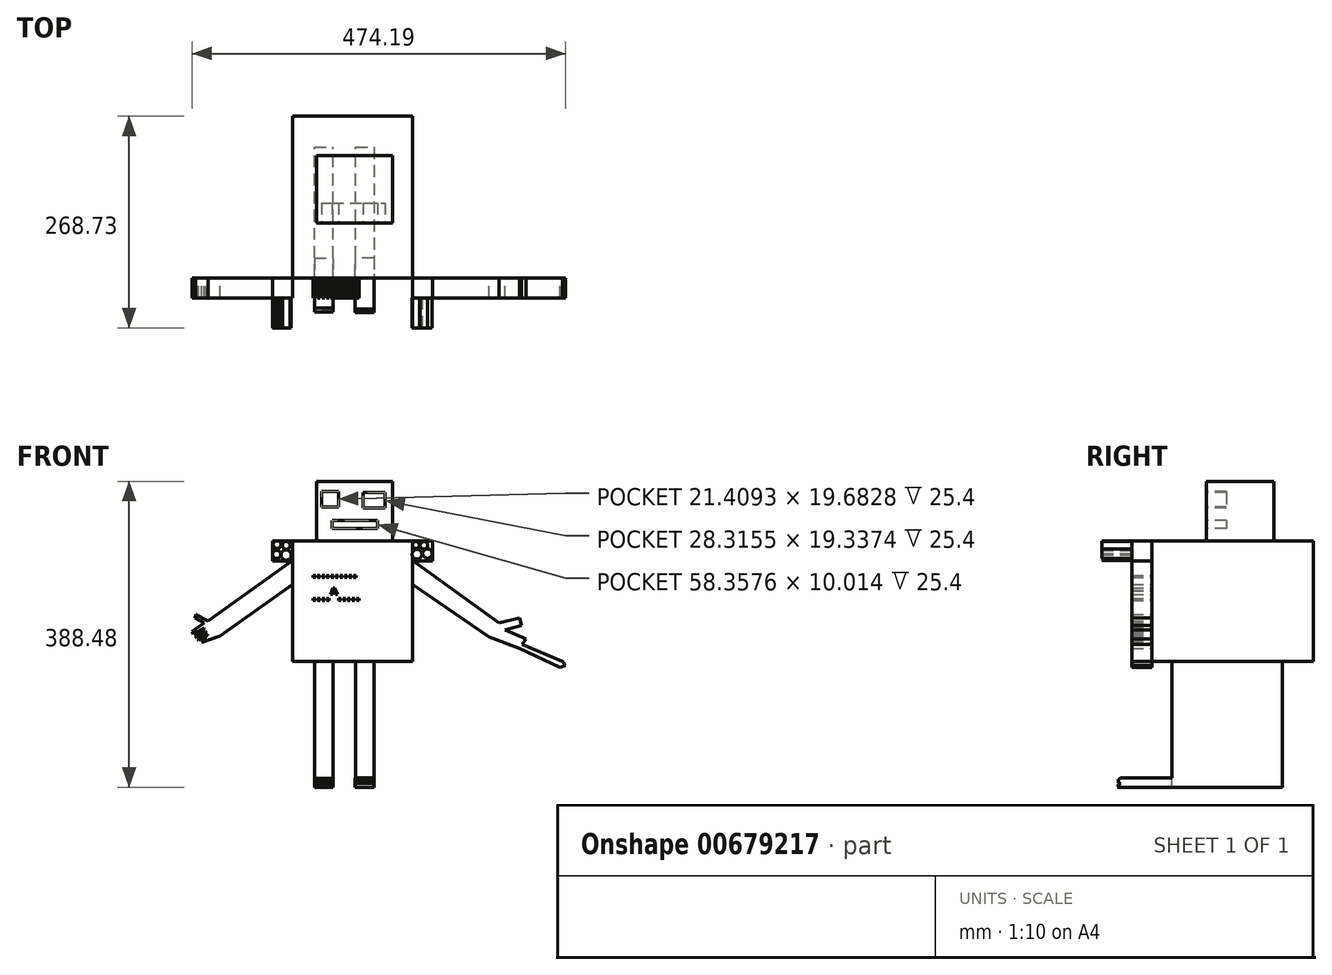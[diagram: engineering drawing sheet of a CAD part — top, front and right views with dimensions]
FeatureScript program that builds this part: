
annotation { "Feature Type Name" : "Feature", "Feature Type Description" : "" }
export const myFeature = defineFeature(function(context is Context, id is Id, definition is map)
    precondition{}
    {
        {
            var Q0;
            Q0=qCreatedBy(makeId("Front.planeOp"),FACE);
            var sketch = newSketch(context, id + "F0", { "sketchPlane" : qUnion([Q0])});
            skLineSegment(sketch, "E0.bottom", {"start": v(-75.78, 76.02) * mm, "end": v(76.26, 76.02) * mm});
            skLineSegment(sketch, "E0.top", {"start": v(-75.78, -76.75) * mm, "end": v(76.26, -76.75) * mm});
            skLineSegment(sketch, "E0.left", {"start": v(-75.78, 76.02) * mm, "end": v(-75.78, -76.75) * mm});
            skLineSegment(sketch, "E0.right", {"start": v(76.26, 76.02) * mm, "end": v(76.26, -76.75) * mm});
            skSolve(sketch);
        }
        {
            var Q0;
            Q0=makeQuery(id+"F0.imprint","IMPRINT",FACE,{"disambiguationData":[TD([[makeQuery(id+"F0.imprint","IMPRINT",EDGE,{"derivedFrom":sQuery(id+"F0.wireOp",EDGE,"E0.bottom")}),-1.0]])]});
            extrude(context, id + "F1", {"entities" : qUnion([Q0]), "depth" : 205.23 * mm, "offsetDistance" : 25.4 * mm});
        }
        {
            var Q0;
            Q0=makeQuery(id+"F1.opExtrude","CAP_FACE",FACE,{"disambiguationData":[OSD([sQuery(id+"F0.wireOp",EDGE,"E0.bottom"),sQuery(id+"F0.wireOp",EDGE,"E0.top"),sQuery(id+"F0.wireOp",EDGE,"E0.left"),sQuery(id+"F0.wireOp",EDGE,"E0.right")])],"isStart":false});
            var sketch = newSketch(context, id + "F2", { "sketchPlane" : qUnion([Q0])});
            skLineSegment(sketch, "E1", {"start": v(-75.78, 76.02) * mm, "end": v(-101.18, 76.02) * mm});
            skLineSegment(sketch, "E2", {"start": v(-101.18, 50.62) * mm, "end": v(-101.18, 76.02) * mm});
            skLineSegment(sketch, "E3", {"start": v(-101.18, 50.62) * mm, "end": v(-75.78, 50.62) * mm});
            skLineSegment(sketch, "E4", {"start": v(-75.78, 50.62) * mm, "end": v(-75.78, 50.62) * mm});
            skLineSegment(sketch, "E5", {"start": v(-75.78, 50.62) * mm, "end": v(-75.78, 76.02) * mm});
            skLineSegment(sketch, "E6", {"start": v(76.26, 76.02) * mm, "end": v(101.66, 76.02) * mm});
            skLineSegment(sketch, "E7", {"start": v(101.66, 76.02) * mm, "end": v(101.66, 50.62) * mm});
            skLineSegment(sketch, "E8", {"start": v(101.66, 50.62) * mm, "end": v(76.26, 50.62) * mm});
            skLineSegment(sketch, "E9", {"start": v(76.26, 50.62) * mm, "end": v(76.26, 76.02) * mm});
            skSolve(sketch);
        }
        {
            var Q0;
            Q0=makeQuery(id+"F2.imprint","IMPRINT",FACE,{"disambiguationData":[TD([[makeQuery(id+"F2.imprint","IMPRINT",EDGE,{"derivedFrom":sQuery(id+"F2.wireOp",EDGE,"E1")}),1.0]])]});
            var Q1;
            Q1=makeQuery(id+"F2.imprint","IMPRINT",FACE,{"disambiguationData":[TD([[makeQuery(id+"F2.imprint","IMPRINT",EDGE,{"derivedFrom":sQuery(id+"F2.wireOp",EDGE,"E6")}),-1.0]])]});
            extrude(context, id + "F3", {"entities" : qUnion([Q0, Q1]), "depth" : 25.4 * mm, "offsetDistance" : 25.4 * mm});
        }
        {
            var Q0;
            Q0=makeQuery(id+"F3.opExtrude","CAP_FACE",FACE,{"disambiguationData":[OSD([sQuery(id+"F2.wireOp",EDGE,"E1"),sQuery(id+"F2.wireOp",EDGE,"E2"),sQuery(id+"F2.wireOp",EDGE,"E3"),sQuery(id+"F2.wireOp",EDGE,"E5")])],"isStart":false});
            var sketch = newSketch(context, id + "F4", { "sketchPlane" : qUnion([Q0])});
            skCircle(sketch, "E10", {"center": v(-95.6, 71.34) * mm, "radius": 4.89 * mm});
            skCircle(sketch, "E11", {"center": v(-84.03, 70.36) * mm, "radius": 4.92 * mm});
            skCircle(sketch, "E12", {"center": v(-96.09, 59.03) * mm, "radius": 5.18 * mm});
            skCircle(sketch, "E13", {"center": v(-84.03, 58.05) * mm, "radius": 6.5 * mm});
            skCircle(sketch, "E14", {"center": v(80.67, 70.85) * mm, "radius": 4.44 * mm});
            skCircle(sketch, "E15", {"center": v(91.01, 70.36) * mm, "radius": 4.78 * mm});
            skCircle(sketch, "E16", {"center": v(82.15, 59.03) * mm, "radius": 6.12 * mm});
            skCircle(sketch, "E17", {"center": v(95.44, 60.02) * mm, "radius": 6 * mm});
            skSolve(sketch);
        }
        {
            var Q0;
            {var subQ0=sQuery(id+"F4.wireOp",EDGE,"E10");var subQ1=makeQuery(id+"F3.opExtrude","CAP_EDGE",EDGE,{"disambiguationData":[OSD([sQuery(id+"F2.wireOp",EDGE,"E1")])],"isStart":false});var subQ2=makeQuery(id+"F4.imprint","INTERSECT",VERTEX,{"disambiguationData":[OD(0.0)],"derivedFrom":[subQ1,subQ0]});Q0=makeQuery(id+"F4.imprint","IMPRINT",FACE,{"disambiguationData":[TD([[makeQuery(id+"F4.imprint","IMPRINT",EDGE,{"disambiguationData":[TD([[subQ2,1.0]])],"derivedFrom":subQ0}),1.0]])]});}
            var Q1;
            {var subQ0=sQuery(id+"F4.wireOp",EDGE,"E12");var subQ1=makeQuery(id+"F3.opExtrude","CAP_EDGE",EDGE,{"disambiguationData":[OSD([sQuery(id+"F2.wireOp",EDGE,"E2")])],"isStart":false});var subQ2=makeQuery(id+"F4.imprint","INTERSECT",VERTEX,{"disambiguationData":[OD(0.0)],"derivedFrom":[subQ1,subQ0]});Q1=makeQuery(id+"F4.imprint","IMPRINT",FACE,{"disambiguationData":[TD([[makeQuery(id+"F4.imprint","IMPRINT",EDGE,{"disambiguationData":[TD([[subQ2,1.0]])],"derivedFrom":subQ0}),1.0]])]});}
            var Q2;
            Q2=makeQuery(id+"F4.imprint","IMPRINT",FACE,{"disambiguationData":[TD([[makeQuery(id+"F4.imprint","IMPRINT",EDGE,{"derivedFrom":sQuery(id+"F4.wireOp",EDGE,"E13")}),1.0]])]});
            var Q3;
            Q3=makeQuery(id+"F4.imprint","IMPRINT",FACE,{"disambiguationData":[TD([[makeQuery(id+"F4.imprint","IMPRINT",EDGE,{"derivedFrom":sQuery(id+"F4.wireOp",EDGE,"E11")}),1.0]])]});
            var Q4;
            Q4=makeQuery(id+"F4.imprint","IMPRINT",FACE,{"disambiguationData":[TD([[makeQuery(id+"F4.imprint","IMPRINT",EDGE,{"derivedFrom":sQuery(id+"F4.wireOp",EDGE,"E14")}),1.0]])]});
            var Q5;
            Q5=makeQuery(id+"F4.imprint","IMPRINT",FACE,{"disambiguationData":[TD([[makeQuery(id+"F4.imprint","IMPRINT",EDGE,{"derivedFrom":sQuery(id+"F4.wireOp",EDGE,"E16")}),1.0]])]});
            var Q6;
            Q6=makeQuery(id+"F4.imprint","IMPRINT",FACE,{"disambiguationData":[TD([[makeQuery(id+"F4.imprint","IMPRINT",EDGE,{"derivedFrom":sQuery(id+"F4.wireOp",EDGE,"E15")}),1.0]])]});
            var Q7;
            Q7=makeQuery(id+"F4.imprint","IMPRINT",FACE,{"disambiguationData":[TD([[makeQuery(id+"F4.imprint","IMPRINT",EDGE,{"derivedFrom":sQuery(id+"F4.wireOp",EDGE,"E17")}),1.0]])]});
            extrude(context, id + "F5", {"entities" : qUnion([Q0, Q1, Q2, Q3, Q4, Q5, Q6, Q7]), "depth" : 38.1 * mm, "offsetDistance" : 25.4 * mm});
        }
        {
            var Q0;
            Q0=makeQuery(id+"F1.opExtrude","CAP_FACE",FACE,{"disambiguationData":[OSD([sQuery(id+"F0.wireOp",EDGE,"E0.bottom"),sQuery(id+"F0.wireOp",EDGE,"E0.top"),sQuery(id+"F0.wireOp",EDGE,"E0.left"),sQuery(id+"F0.wireOp",EDGE,"E0.right")])],"isStart":false});
            var sketch = newSketch(context, id + "F6", { "sketchPlane" : qUnion([Q0])});
            skText(sketch, "E18", { "text": "..........\n....^.....", "fontName": "RobotoSlab-Bold.ttf"});
            const initialGuessF6  = {"E18": [-0.051, 0.02956, 1, 0, 0.016]};
            skSetInitialGuess(sketch, initialGuessF6);
            skSolve(sketch);
        }
        {
            var Q0;
            Q0 = qSketchRegion(id + "F6", true);
            extrude(context, id + "F7", {"entities" : qUnion([Q0]), "operationType" : NewBodyOperationType.ADD, "depth" : 25.4 * mm, "offsetDistance" : 25.4 * mm});
        }
        {
            var Q0;
            Q0=makeQuery(id+"F1.opExtrude","SWEPT_FACE",FACE,{"disambiguationData":[OSD([sQuery(id+"F0.wireOp",EDGE,"E0.top")])]});
            var sketch = newSketch(context, id + "F8", { "sketchPlane" : qUnion([Q0])});
            skLineSegment(sketch, "E19", {"start": v(-48.14, 179.76) * mm, "end": v(-48.14, 135.43) * mm});
            skLineSegment(sketch, "E20", {"start": v(-48.14, 179.76) * mm, "end": v(-24.7, 179.76) * mm});
            skLineSegment(sketch, "E21", {"start": v(-24.7, 179.76) * mm, "end": v(-24.7, 39.1) * mm});
            skLineSegment(sketch, "E22", {"start": v(-48.14, 39.1) * mm, "end": v(-48.14, 135.43) * mm});
            skLineSegment(sketch, "E23", {"start": v(-48.14, 39.1) * mm, "end": v(-24.7, 39.1) * mm});
            skLineSegment(sketch, "E24", {"start": v(4.3, 179.76) * mm, "end": v(4.3, 39.1) * mm});
            skLineSegment(sketch, "E25", {"start": v(4.3, 39.1) * mm, "end": v(27.3, 39.1) * mm});
            skLineSegment(sketch, "E26", {"start": v(27.3, 39.1) * mm, "end": v(27.3, 179.76) * mm});
            skLineSegment(sketch, "E27", {"start": v(27.3, 179.76) * mm, "end": v(4.3, 179.76) * mm});
            skSolve(sketch);
        }
        {
            var Q0;
            Q0=makeQuery(id+"F8.imprint","IMPRINT",FACE,{"disambiguationData":[TD([[makeQuery(id+"F8.imprint","IMPRINT",EDGE,{"derivedFrom":sQuery(id+"F8.wireOp",EDGE,"E19")}),1.0]])]});
            var Q1;
            Q1=makeQuery(id+"F8.imprint","IMPRINT",FACE,{"disambiguationData":[TD([[makeQuery(id+"F8.imprint","IMPRINT",EDGE,{"derivedFrom":sQuery(id+"F8.wireOp",EDGE,"E24")}),1.0]])]});
            extrude(context, id + "F9", {"entities" : qUnion([Q0, Q1]), "operationType" : NewBodyOperationType.ADD, "depth" : 160.02 * mm, "offsetDistance" : 25.4 * mm});
        }
        {
            var Q0;
            Q0=makeQuery(id+"F9.opExtrude","SWEPT_FACE",FACE,{"disambiguationData":[OSD([sQuery(id+"F8.wireOp",EDGE,"E26")])]});
            var sketch = newSketch(context, id + "F10", { "sketchPlane" : qUnion([Q0])});
            skLineSegment(sketch, "E28", {"start": v(-176.13, -225.1) * mm, "end": v(-245.06, -225.1) * mm});
            skLineSegment(sketch, "E29", {"start": v(-245.06, -225.1) * mm, "end": v(-248.62, -229.17) * mm});
            skLineSegment(sketch, "E30", {"start": v(-248.62, -229.17) * mm, "end": v(-245.06, -232.28) * mm});
            skLineSegment(sketch, "E31", {"start": v(-245.06, -232.28) * mm, "end": v(-248.98, -236.77) * mm});
            skLineSegment(sketch, "E32", {"start": v(-248.98, -236.77) * mm, "end": v(-179.76, -236.77) * mm});
            skLineSegment(sketch, "E33", {"start": v(-179.76, -236.77) * mm, "end": v(-176.13, -225.1) * mm});
            skSolve(sketch);
        }
        {
            var Q0;
            {var subQ0=sQuery(id+"F10.wireOp",EDGE,"E29");Q0=makeQuery(id+"F10.imprint","IMPRINT",FACE,{"disambiguationData":[TD([[makeQuery(id+"F10.imprint","IMPRINT",EDGE,{"derivedFrom":subQ0}),1.0]])]});}
            extrude(context, id + "F11", {"entities" : qUnion([Q0]), "operationType" : NewBodyOperationType.ADD, "oppositeDirection" : true, "depth" : 24.13 * mm, "offsetDistance" : 25.4 * mm});
        }
        {
            var Q0;
            Q0=makeQuery(id+"F9.opExtrude","SWEPT_FACE",FACE,{"disambiguationData":[OSD([sQuery(id+"F8.wireOp",EDGE,"E19"),sQuery(id+"F8.wireOp",EDGE,"E22")])]});
            var sketch = newSketch(context, id + "F12", { "sketchPlane" : qUnion([Q0])});
            skLineSegment(sketch, "E34", {"start": v(177.82, -225.49) * mm, "end": v(243.67, -225.49) * mm});
            skLineSegment(sketch, "E35", {"start": v(243.67, -225.49) * mm, "end": v(248.67, -228.82) * mm});
            skLineSegment(sketch, "E36", {"start": v(248.67, -228.82) * mm, "end": v(245.72, -233.24) * mm});
            skLineSegment(sketch, "E37", {"start": v(245.72, -233.24) * mm, "end": v(248.67, -235.21) * mm});
            skLineSegment(sketch, "E38", {"start": v(248.67, -235.21) * mm, "end": v(179.76, -236.77) * mm});
            skLineSegment(sketch, "E39", {"start": v(179.76, -236.77) * mm, "end": v(177.82, -225.49) * mm});
            skSolve(sketch);
        }
        {
            var Q0;
            {var subQ0=sQuery(id+"F12.wireOp",EDGE,"E35");Q0=makeQuery(id+"F12.imprint","IMPRINT",FACE,{"disambiguationData":[TD([[makeQuery(id+"F12.imprint","IMPRINT",EDGE,{"derivedFrom":subQ0}),-1.0]])]});}
            extrude(context, id + "F13", {"entities" : qUnion([Q0]), "operationType" : NewBodyOperationType.ADD, "oppositeDirection" : true, "depth" : 23.88 * mm, "offsetDistance" : 25.4 * mm});
        }
        {
            var Q0;
            Q0=makeQuery(id+"F1.opExtrude","SWEPT_FACE",FACE,{"disambiguationData":[OSD([sQuery(id+"F0.wireOp",EDGE,"E0.bottom")])]});
            var sketch = newSketch(context, id + "F14", { "sketchPlane" : qUnion([Q0])});
            skLineSegment(sketch, "E40.bottom", {"start": v(-45.76, -49.95) * mm, "end": v(51.15, -49.95) * mm});
            skLineSegment(sketch, "E40.top", {"start": v(-45.76, -135.53) * mm, "end": v(51.15, -135.53) * mm});
            skLineSegment(sketch, "E40.left", {"start": v(-45.76, -49.95) * mm, "end": v(-45.76, -135.53) * mm});
            skLineSegment(sketch, "E40.right", {"start": v(51.15, -49.95) * mm, "end": v(51.15, -135.53) * mm});
            skSolve(sketch);
        }
        {
            var Q0;
            Q0=makeQuery(id+"F14.imprint","IMPRINT",FACE,{"disambiguationData":[TD([[makeQuery(id+"F14.imprint","IMPRINT",EDGE,{"derivedFrom":sQuery(id+"F14.wireOp",EDGE,"E40.bottom")}),-1.0]])]});
            extrude(context, id + "F15", {"entities" : qUnion([Q0]), "operationType" : NewBodyOperationType.ADD, "depth" : 75.7 * mm, "offsetDistance" : 25.4 * mm});
        }
        {
            var Q0;
            Q0=makeQuery(id+"F15.opExtrude","SWEPT_FACE",FACE,{"disambiguationData":[OSD([sQuery(id+"F14.wireOp",EDGE,"E40.top")])]});
            var sketch = newSketch(context, id + "F16", { "sketchPlane" : qUnion([Q0])});
            skLineSegment(sketch, "E41.bottom", {"start": v(-39.15, 139.13) * mm, "end": v(-17.74, 139.13) * mm});
            skLineSegment(sketch, "E41.top", {"start": v(-39.15, 119.44) * mm, "end": v(-17.74, 119.44) * mm});
            skLineSegment(sketch, "E41.left", {"start": v(-39.15, 139.13) * mm, "end": v(-39.15, 119.44) * mm});
            skLineSegment(sketch, "E41.right", {"start": v(-17.74, 139.13) * mm, "end": v(-17.74, 119.44) * mm});
            skLineSegment(sketch, "E42.bottom", {"start": v(13.34, 137.4) * mm, "end": v(41.66, 137.4) * mm});
            skLineSegment(sketch, "E42.top", {"start": v(13.34, 118.06) * mm, "end": v(41.66, 118.06) * mm});
            skLineSegment(sketch, "E42.left", {"start": v(13.34, 137.4) * mm, "end": v(13.34, 118.06) * mm});
            skLineSegment(sketch, "E42.right", {"start": v(41.66, 137.4) * mm, "end": v(41.66, 118.06) * mm});
            skLineSegment(sketch, "E43.bottom", {"start": v(-26.02, 102.18) * mm, "end": v(32.33, 102.18) * mm});
            skLineSegment(sketch, "E43.top", {"start": v(-26.02, 92.16) * mm, "end": v(32.33, 92.16) * mm});
            skLineSegment(sketch, "E43.left", {"start": v(-26.02, 102.18) * mm, "end": v(-26.02, 92.16) * mm});
            skLineSegment(sketch, "E43.right", {"start": v(32.33, 102.18) * mm, "end": v(32.33, 92.16) * mm});
            skSolve(sketch);
        }
        {
            var Q0;
            Q0=makeQuery(id+"F16.imprint","IMPRINT",FACE,{"disambiguationData":[TD([[makeQuery(id+"F16.imprint","IMPRINT",EDGE,{"derivedFrom":sQuery(id+"F16.wireOp",EDGE,"E41.bottom")}),-1.0]])]});
            var Q1;
            Q1=makeQuery(id+"F16.imprint","IMPRINT",FACE,{"disambiguationData":[TD([[makeQuery(id+"F16.imprint","IMPRINT",EDGE,{"derivedFrom":sQuery(id+"F16.wireOp",EDGE,"E42.bottom")}),-1.0]])]});
            var Q2;
            Q2=makeQuery(id+"F16.imprint","IMPRINT",FACE,{"disambiguationData":[TD([[makeQuery(id+"F16.imprint","IMPRINT",EDGE,{"derivedFrom":sQuery(id+"F16.wireOp",EDGE,"E43.bottom")}),-1.0]])]});
            extrude(context, id + "F17", {"entities" : qUnion([Q0, Q1, Q2]), "operationType" : NewBodyOperationType.REMOVE, "oppositeDirection" : true, "depth" : 25.4 * mm, "offsetDistance" : 25.4 * mm});
        }
        {
            var Q0;
            Q0=makeQuery(id+"F1.opExtrude","CAP_FACE",FACE,{"disambiguationData":[OSD([sQuery(id+"F0.wireOp",EDGE,"E0.bottom"),sQuery(id+"F0.wireOp",EDGE,"E0.top"),sQuery(id+"F0.wireOp",EDGE,"E0.left"),sQuery(id+"F0.wireOp",EDGE,"E0.right")])],"isStart":false});
            var sketch = newSketch(context, id + "F18", { "sketchPlane" : qUnion([Q0])});
            skLineSegment(sketch, "E44", {"start": v(-75.78, 51.25) * mm, "end": v(-183.4, -25.82) * mm});
            skLineSegment(sketch, "E45", {"start": v(-183.4, -25.82) * mm, "end": v(-169.02, -45.9) * mm});
            skLineSegment(sketch, "E46", {"start": v(-168.22, -44.79) * mm, "end": v(-75.78, 20.6) * mm});
            skLineSegment(sketch, "E47", {"start": v(-183.4, -25.82) * mm, "end": v(-198.82, -17.33) * mm});
            skLineSegment(sketch, "E48", {"start": v(-198.82, -17.33) * mm, "end": v(-199.93, -21.65) * mm});
            skLineSegment(sketch, "E49", {"start": v(-199.93, -21.65) * mm, "end": v(-188.52, -28.41) * mm});
            skLineSegment(sketch, "E50", {"start": v(-188.52, -28.41) * mm, "end": v(-203.49, -39.13) * mm});
            skLineSegment(sketch, "E51", {"start": v(-203.49, -39.13) * mm, "end": v(-201.42, -42.01) * mm});
            skLineSegment(sketch, "E52", {"start": v(-201.42, -42.01) * mm, "end": v(-188.52, -34.3) * mm});
            skLineSegment(sketch, "E53", {"start": v(-188.52, -34.3) * mm, "end": v(-187.41, -35.84) * mm});
            skLineSegment(sketch, "E54", {"start": v(-187.41, -35.84) * mm, "end": v(-199.9, -44.79) * mm});
            skLineSegment(sketch, "E55", {"start": v(-199.9, -44.79) * mm, "end": v(-198.1, -47.31) * mm});
            skLineSegment(sketch, "E56", {"start": v(-198.1, -47.31) * mm, "end": v(-186.67, -39.13) * mm});
            skLineSegment(sketch, "E57", {"start": v(-186.67, -39.13) * mm, "end": v(-185.47, -40.8) * mm});
            skLineSegment(sketch, "E58", {"start": v(-185.47, -40.8) * mm, "end": v(-196.5, -48.7) * mm});
            skLineSegment(sketch, "E59", {"start": v(-196.5, -48.7) * mm, "end": v(-195.15, -50.6) * mm});
            skLineSegment(sketch, "E60", {"start": v(-195.15, -50.6) * mm, "end": v(-183.4, -42.18) * mm});
            skLineSegment(sketch, "E61", {"start": v(-183.4, -42.18) * mm, "end": v(-191.24, -53.16) * mm});
            skLineSegment(sketch, "E62", {"start": v(-191.24, -53.16) * mm, "end": v(-168.22, -44.79) * mm});
            skLineSegment(sketch, "E63", {"start": v(76.26, 51.25) * mm, "end": v(186.2, -28.41) * mm});
            skLineSegment(sketch, "E64", {"start": v(186.2, -28.41) * mm, "end": v(173.53, -45.9) * mm});
            skLineSegment(sketch, "E65", {"start": v(173.53, -45.9) * mm, "end": v(76.26, 20.6) * mm});
            skLineSegment(sketch, "E66", {"start": v(76.26, 20.6) * mm, "end": v(76.26, 51.25) * mm});
            skLineSegment(sketch, "E67", {"start": v(186.2, -28.41) * mm, "end": v(212.58, -21.65) * mm});
            skLineSegment(sketch, "E68", {"start": v(212.58, -21.65) * mm, "end": v(215.09, -31.46) * mm});
            skLineSegment(sketch, "E69", {"start": v(215.09, -31.46) * mm, "end": v(194.12, -36.83) * mm});
            skLineSegment(sketch, "E70", {"start": v(194.12, -36.83) * mm, "end": v(220.51, -48.7) * mm});
            skLineSegment(sketch, "E71", {"start": v(220.51, -48.7) * mm, "end": v(219.15, -50.6) * mm});
            skLineSegment(sketch, "E72", {"start": v(219.15, -50.6) * mm, "end": v(212.1, -60.32) * mm});
            skLineSegment(sketch, "E73", {"start": v(212.1, -60.32) * mm, "end": v(173.53, -45.9) * mm});
            skLineSegment(sketch, "E74", {"start": v(215.62, -55.45) * mm, "end": v(266.98, -76.75) * mm});
            skLineSegment(sketch, "E75", {"start": v(266.98, -76.75) * mm, "end": v(270.7, -81.95) * mm});
            skLineSegment(sketch, "E76", {"start": v(270.7, -81.95) * mm, "end": v(264.04, -84.37) * mm});
            skLineSegment(sketch, "E77", {"start": v(264.04, -84.37) * mm, "end": v(212.1, -60.32) * mm});
            skSolve(sketch);
        }
        {
            var Q0;
            {var subQ0=sQuery(id+"F18.wireOp",EDGE,"E47");Q0=makeQuery(id+"F18.imprint","IMPRINT",FACE,{"disambiguationData":[TD([[makeQuery(id+"F18.imprint","IMPRINT",EDGE,{"derivedFrom":subQ0}),1.0]])]});}
            var Q1;
            {var subQ4=sQuery(id+"F18.wireOp",EDGE,"E44");Q1=makeQuery(id+"F18.imprint","IMPRINT",FACE,{"disambiguationData":[TD([[makeQuery(id+"F18.imprint","IMPRINT",EDGE,{"derivedFrom":subQ4}),1.0]])]});}
            var Q2;
            Q2=makeQuery(id+"F18.imprint","IMPRINT",FACE,{"disambiguationData":[TD([[makeQuery(id+"F18.imprint","IMPRINT",EDGE,{"derivedFrom":sQuery(id+"F18.wireOp",EDGE,"E63")}),-1.0]])]});
            var Q3;
            Q3=makeQuery(id+"F18.imprint","IMPRINT",FACE,{"disambiguationData":[TD([[makeQuery(id+"F18.imprint","IMPRINT",EDGE,{"derivedFrom":sQuery(id+"F18.wireOp",EDGE,"E64")}),1.0]])]});
            var Q4;
            {var subQ0=sQuery(id+"F18.wireOp",EDGE,"E74");Q4=makeQuery(id+"F18.imprint","IMPRINT",FACE,{"disambiguationData":[TD([[makeQuery(id+"F18.imprint","IMPRINT",EDGE,{"derivedFrom":subQ0}),-1.0]])]});}
            extrude(context, id + "F19", {"entities" : qUnion([Q0, Q1, Q2, Q3, Q4]), "depth" : 25.4 * mm, "offsetDistance" : 25.4 * mm});
        }
    });
